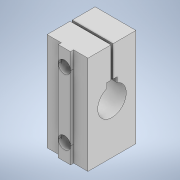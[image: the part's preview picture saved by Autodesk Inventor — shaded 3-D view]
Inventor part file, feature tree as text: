
AUTODESK INVENTOR PART (.ipt)
format: ipt  version: 2021 (Build 250183000, 183)  size: 165,888 bytes
history: native  units: mm
features: projected_geometry x5, extrude x4, sketch x4
ambient origin geometry x8: Origin, YZ Plane, XZ Plane, XY Plane, X Axis, Y Axis, Z Axis, Center Point
bodies: Solid1 (feature_tree)
feature tree (13):
  extrude  "Extrusion1"  Depth=48.0mm
  extrude  "Extrusion2"  Depth=3.0mm
  extrude  "Extrusion3"  Depth=1.5mm TaperAngle=0.0deg
  extrude  "Extrusion4"  Depth=5.0mm
  sketch  "Sketch1"  dims[d0=20.0mm d1=48.0mm]
  sketch  "Sketch2"  dims[d2=25.0mm d3=0.0mm d4=3.0mm]
  projected_geometry  "Projected Loop1"
  sketch  "Sketch3"  dims[d5=3.0mm d6=1.5mm d7=0.0mm]
  projected_geometry  "Projected Loop2"
  sketch  "Sketch4"  dims[d8=14.0mm d9=5.0mm d10=5.0mm d11=11.0mm d12=0.5mm d13=0.5mm d14=0.0mm d15=0.0mm d16=6.0mm d17=6.0mm d18=8.0mm d19=8.0mm d20=4.0mm d21=0.0mm]
  projected_geometry  "Projected Loop3"
  projected_geometry  "Projected Loop4"
  projected_geometry  "Projected Loop5"
